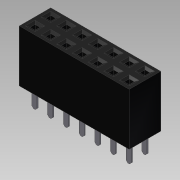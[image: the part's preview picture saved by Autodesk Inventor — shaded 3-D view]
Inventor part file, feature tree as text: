
AUTODESK INVENTOR PART (.ipt)
format: ipt  version: 2011 (Build 150239000, 239)  size: 262,144 bytes
history: native  units: mm
features: sketch x6, extrude x4, other x2, pattern_linear x2, loft x1, projected_geometry x1
ambient origin geometry x8: Origin, YZ Plane, XZ Plane, XY Plane, X Axis, Y Axis, Z Axis, Center Point
feature tree (16):
  other  "Твердое тело1"
  extrude  "Выдавливание1"  Depth=17.78mm
  extrude  "Выдавливание2"  Depth=5.08mm
  extrude  "Выдавливание3"  Depth=8.89mm
  pattern_linear  "Прямоуг.массив1"  Spacing1=2.54mm  [1 undecoded]
  sketch  "Эскиз4"
  other  "РабПлоскость1"
  loft  "По сечениям1"
  extrude  "Выдавливание4"  Depth=0.2mm
  pattern_linear  "Прямоуг.массив2"  Spacing1=0.8mm  [1 undecoded]
  sketch  "Эскиз1"
  sketch  "Эскиз2"
  sketch  "Эскиз3"
  projected_geometry  "Спроецированная петля1"
  sketch  "Эскиз5"
  sketch  "Эскиз6"
note: 2 required parameter values undecoded (feature->parameter linkage not recoverable at this tier; creation-order binding heuristic only, values carry confidence <= 0.55)
